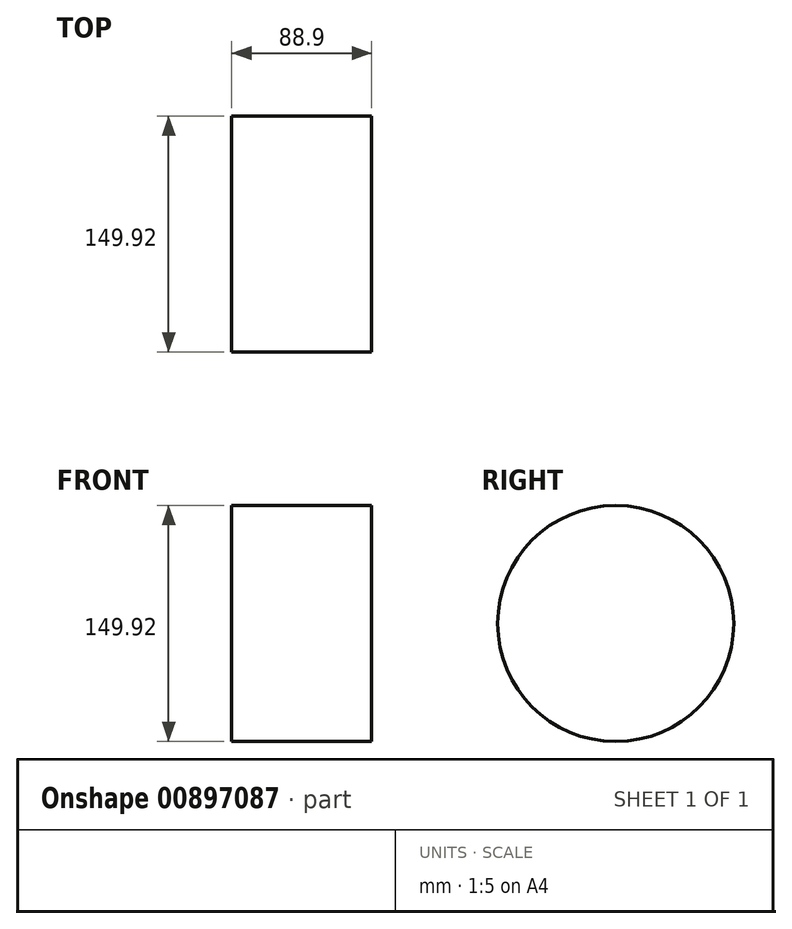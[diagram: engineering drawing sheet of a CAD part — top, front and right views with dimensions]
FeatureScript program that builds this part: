
annotation { "Feature Type Name" : "Feature", "Feature Type Description" : "" }
export const myFeature = defineFeature(function(context is Context, id is Id, definition is map)
    precondition{}
    {
        {
            var Q0;
            Q0=qCreatedBy(makeId("Right.planeOp"),FACE);
            var sketch = newSketch(context, id + "F0", { "sketchPlane" : qUnion([Q0])});
            skCircle(sketch, "E0", {"center": v(0, 0) * mm, "radius": 74.96 * mm});
            skSolve(sketch);
        }
        {
            var Q0;
            Q0=makeQuery(id+"F0.imprint","IMPRINT",FACE,{"disambiguationData":[TD([[makeQuery(id+"F0.imprint","IMPRINT",EDGE,{"derivedFrom":sQuery(id+"F0.wireOp",EDGE,"E0")}),1.0]])]});
            extrude(context, id + "F1", {"entities" : qUnion([Q0]), "depth" : 88.9 * mm, "offsetDistance" : 25.4 * mm});
        }
    });
